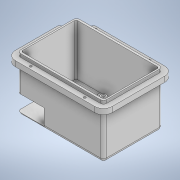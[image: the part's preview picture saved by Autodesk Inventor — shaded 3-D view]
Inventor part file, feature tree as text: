
AUTODESK INVENTOR PART (.ipt)
format: ipt  version: 2021 (Build 250183000, 183)  size: 444,416 bytes
history: native  units: mm
features: sketch x12, extrude x10, projected_geometry x7, fillet x6, other x4, chamfer x2, plane x2, hole x1
ambient origin geometry x8: Origin, YZ Plane, XZ Plane, XY Plane, X Axis, Y Axis, Z Axis, Center Point
bodies: Body1 (feature_tree)
feature tree (44):
  other  "實體1"
  extrude  "擠出1"  Depth=154.0mm
  fillet  "圓角1"  Radius=102.0mm
  fillet  "圓角2"  Radius=159.8mm
  extrude  "擠出2"  Depth=109.8mm
  chamfer  "倒角1"  Distance=95.0mm
  fillet  "圓角3"  Radius=2.9mm
  plane  "工作平面1"
  extrude  "擠出3"  Depth=6.0mm
  hole  "孔1"  [1 undecoded]
  extrude  "擠出7"  Depth=2.9mm
  fillet  "圓角5"  [1 undecoded]
  extrude  "擠出8"  Depth=2.0mm TaperAngle=45.0deg
  extrude  "擠出9"  Depth=6.0mm
  extrude  "擠出10"  [1 undecoded]
  extrude  "擠出11"  Depth=10.0mm
  fillet  "圓角6"  Radius=10.0mm
  plane  "工作平面2"
  sketch  "草圖13"
  other  "凸轂1"
  other  "凸轂2"
  extrude  "擠出12"  Depth=30.0mm
  fillet  "圓角7"  Radius=15.0mm
  chamfer  "倒角2"  Distance=5.0mm
  extrude  "擠出13"  Depth=5.0mm
  sketch  "草圖1"
  sketch  "草圖2"
  projected_geometry  "投影迴路1"
  sketch  "草圖3"
  sketch  "草圖7"
  sketch  "草圖8"
  projected_geometry  "投影迴路3"
  sketch  "草圖9"
  sketch  "草圖10"
  sketch  "草圖11"
  projected_geometry  "投影迴路4"
  sketch  "草圖12"
  projected_geometry  "投影迴路5"
  sketch  "草圖14"
  projected_geometry  "投影迴路6"
  projected_geometry  "投影迴路7"
  sketch  "草圖15"
  projected_geometry  "投影迴路8"
  other  "投影切割邊1"
note: 3 required parameter values undecoded (feature->parameter linkage not recoverable at this tier; creation-order binding heuristic only, values carry confidence <= 0.55)
